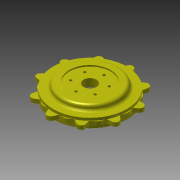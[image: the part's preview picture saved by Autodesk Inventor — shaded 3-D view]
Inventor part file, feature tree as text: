
AUTODESK INVENTOR PART (.ipt)
format: ipt  version: 2015 (Build 190159000, 159)  size: 402,944 bytes
history: native  units: mm
features: extrude x8, sketch x8, pattern_circular x3, fillet x2, pattern_linear x1
ambient origin geometry x8: Origin, YZ Plane, XZ Plane, XY Plane, X Axis, Y Axis, Z Axis, Center Point
bodies: 实体1 (feature_tree)
feature tree (22):
  extrude  "拉伸1"  Depth=25.0mm
  pattern_circular  "环形阵列1"  Count=2  [1 undecoded]
  extrude  "拉伸2"  Depth=40.0mm
  fillet  "圆角1"  Radius=12.0mm
  pattern_circular  "环形阵列2"  Count=6 Angle=180.0deg
  extrude  "拉伸3"  Depth=100.0mm
  pattern_linear  "矩形阵列1"  Count1=10  [1 undecoded]
  extrude  "拉伸4"  Depth=15.0mm TaperAngle=0.0deg
  extrude  "拉伸5"  Depth=100.0mm TaperAngle=360.0deg
  fillet  "圆角2"  Radius=15.0mm
  extrude  "拉伸6"  Depth=24.0mm
  pattern_circular  "环形阵列3"  Count=10 Angle=360.0deg
  extrude  "拉伸7"  Depth=10.0mm TaperAngle=0.0deg
  extrude  "拉伸8"  Depth=20.0mm
  sketch  "草图1"  dims[d0=100.0mm d1=25.0mm]
  sketch  "草图2"  dims[d2=34.0656mm]
  sketch  "草图3"  dims[d3=40.06911mm d4=20.0mm]
  sketch  "草图4"  dims[d5=40.0mm d6=12.0mm d7=12.0mm]
  sketch  "草图5"  dims[d8=12.0mm]
  sketch  "草图6"  dims[d9=12.0mm d10=60.0mm d12=180.0deg]
  sketch  "草图7"  dims[d14=100.0mm d16=360.0deg d18=286.670956mm d19=100.0mm]
  sketch  "草图8"  dims[d20=25.0mm d21=15.0mm d22=0.0mm d23=100.0mm d24=360.0deg d26=15.0mm d27=0.0mm d28=24.0mm d29=100.0mm d30=360.0deg d32=10.0mm d33=0.0mm d34=20.0mm d36=25.0mm d37=220.0mm d38=20.0mm d39=0.0mm d40=160.0mm d41=20.0mm d42=0.0mm d43=10.0mm d44=10.0mm d45=9.899592mm d46=55.0mm d47=20.0mm d48=0.0mm d49=60.0mm d50=360.0deg d52=50.0mm d53=50.0mm d54=0.0mm d55=160.0mm d56=5.0mm d57=0.0mm]
note: 2 required parameter values undecoded (feature->parameter linkage not recoverable at this tier; creation-order binding heuristic only, values carry confidence <= 0.55)
